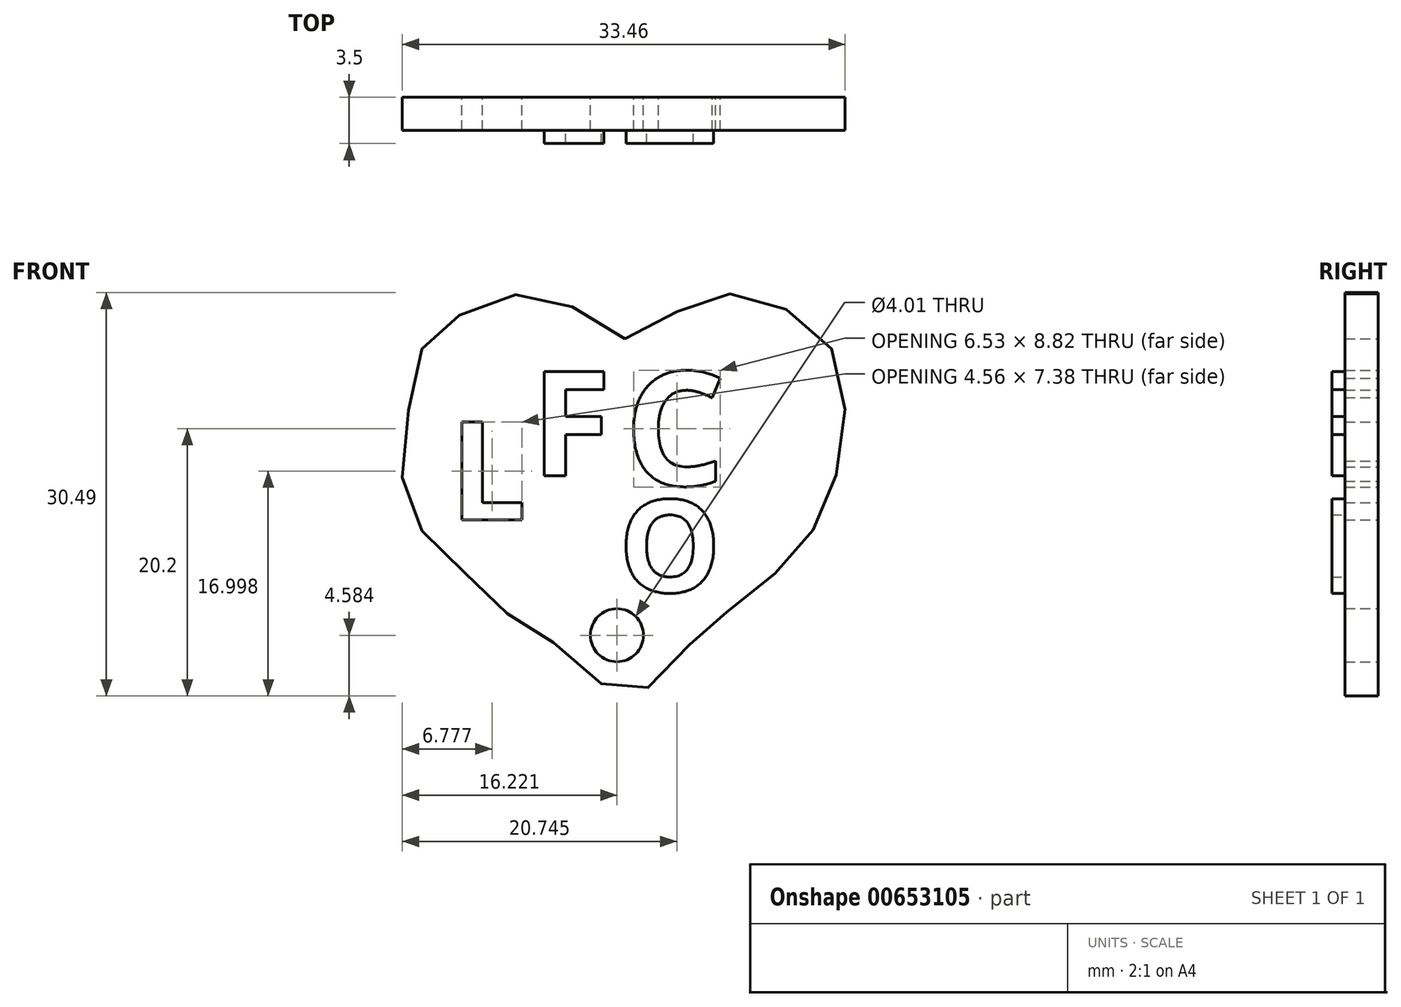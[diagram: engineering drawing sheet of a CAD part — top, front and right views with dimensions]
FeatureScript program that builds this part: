
annotation { "Feature Type Name" : "Feature", "Feature Type Description" : "" }
export const myFeature = defineFeature(function(context is Context, id is Id, definition is map)
    precondition{}
    {
        {
            var Q0;
            Q0=qCreatedBy(makeId("Front.planeOp"),FACE);
            var sketch = newSketch(context, id + "F0", { "sketchPlane" : qUnion([Q0])});
            skPoint(sketch, "E0", {"position": v(-33.54, 35.19) * mm});
            skPoint(sketch, "E1", {"position": v(-38.94, 38.43) * mm});
            skPoint(sketch, "E2", {"position": v(-44.55, 37.56) * mm});
            skPoint(sketch, "E3", {"position": v(-48.44, 35.19) * mm});
            skPoint(sketch, "E4", {"position": v(-49.95, 29.14) * mm});
            skPoint(sketch, "E5", {"position": v(-49.95, 22.44) * mm});
            skPoint(sketch, "E6", {"position": v(-46.28, 18.12) * mm});
            skPoint(sketch, "E7", {"position": v(-42.18, 14.24) * mm});
            skPoint(sketch, "E8", {"position": v(-37.86, 11.43) * mm});
            skPoint(sketch, "E9", {"position": v(-33.32, 8.19) * mm});
            skPoint(sketch, "E10", {"position": v(-29.22, 11.43) * mm});
            skPoint(sketch, "E11", {"position": v(-26.2, 14.24) * mm});
            skPoint(sketch, "E12", {"position": v(-21.44, 18.12) * mm});
            skPoint(sketch, "E13", {"position": v(-18.42, 22.44) * mm});
            skPoint(sketch, "E14", {"position": v(-16.9, 29.14) * mm});
            skPoint(sketch, "E15", {"position": v(-18.42, 35.19) * mm});
            skPoint(sketch, "E16", {"position": v(-28.35, 38) * mm});
            skPoint(sketch, "E17", {"position": v(-23.6, 38.21) * mm});
            skFitSpline(sketch, "E18", {"points": [v(-33.54, 35.19) * mm, v(-38.94, 38.43) * mm, v(-44.55, 37.56) * mm, v(-48.44, 35.19) * mm, v(-49.95, 29.14) * mm, v(-49.95, 22.44) * mm, v(-46.28, 18.12) * mm, v(-42.18, 14.24) * mm, v(-37.86, 11.43) * mm, v(-33.32, 8.19) * mm, v(-29.22, 11.43) * mm, v(-26.2, 14.24) * mm, v(-21.44, 18.12) * mm, v(-18.42, 22.44) * mm, v(-16.9, 29.14) * mm, v(-18.42, 35.19) * mm, v(-23.6, 38.21) * mm, v(-28.35, 38) * mm, v(-33.54, 35.19) * mm]});
            skSolve(sketch);
        }
        {
            var Q0;
            Q0 = qSketchRegion(id + "F0", true);
            extrude(context, id + "F1", {"entities" : qUnion([Q0]), "depth" : 2.5 * mm, "offsetDistance" : 25.4 * mm});
        }
        {
            var Q0;
            Q0=qCreatedBy(makeId("Front.planeOp"),FACE);
            var sketch = newSketch(context, id + "F2", { "sketchPlane" : qUnion([Q0])});
            skText(sketch, "E19", { "text": "F", "fontName": "OpenSans-Bold.ttf"});
            const initialGuessF2  = {"E19": [-0.04063, 0.02482, 1, 0, 0.00796]};
            skSetInitialGuess(sketch, initialGuessF2);
            skSolve(sketch);
        }
        {
            var Q0;
            Q0 = qSketchRegion(id + "F2", true);
            extrude(context, id + "F3", {"entities" : qUnion([Q0]), "operationType" : NewBodyOperationType.ADD, "depth" : 3.5 * mm, "offsetDistance" : 25.4 * mm});
        }
        {
            var Q0;
            Q0=qCreatedBy(makeId("Front.planeOp"),FACE);
            var sketch = newSketch(context, id + "F4", { "sketchPlane" : qUnion([Q0])});
            skText(sketch, "E20", { "text": "L", "fontName": "OpenSans-Bold.ttf"});
            const initialGuessF4  = {"E20": [-0.04678, 0.0215, 1, 0, 0.00744]};
            skSetInitialGuess(sketch, initialGuessF4);
            skSolve(sketch);
        }
        {
            var Q0;
            Q0 = qSketchRegion(id + "F4", true);
            extrude(context, id + "F5", {"entities" : qUnion([Q0]), "operationType" : NewBodyOperationType.REMOVE, "endBound" : BoundingType.UP_TO_NEXT, "depth" : 25.4 * mm, "offsetDistance" : 25.4 * mm});
        }
        {
            var Q0;
            Q0=qCreatedBy(makeId("Front.planeOp"),FACE);
            var sketch = newSketch(context, id + "F6", { "sketchPlane" : qUnion([Q0])});
            skText(sketch, "E21", { "text": "C", "fontName": "OpenSans-Bold.ttf"});
            const initialGuessF6  = {"E21": [-0.03357, 0.0241, 1, 0, 0.00865]};
            skSetInitialGuess(sketch, initialGuessF6);
            skSolve(sketch);
        }
        {
            var Q0;
            Q0 = qSketchRegion(id + "F6", true);
            extrude(context, id + "F7", {"entities" : qUnion([Q0]), "operationType" : NewBodyOperationType.REMOVE, "endBound" : BoundingType.UP_TO_NEXT, "depth" : 25.4 * mm, "offsetDistance" : 25.4 * mm});
        }
        {
            var Q0;
            Q0=qCreatedBy(makeId("Front.planeOp"),FACE);
            var sketch = newSketch(context, id + "F8", { "sketchPlane" : qUnion([Q0])});
            skText(sketch, "E22", { "text": "O", "fontName": "OpenSans-Bold.ttf"});
            const initialGuessF8  = {"E22": [-0.034, 0.01603, 1, 0, 0.00701]};
            skSetInitialGuess(sketch, initialGuessF8);
            skSolve(sketch);
        }
        {
            var Q0;
            Q0 = qSketchRegion(id + "F8", true);
            extrude(context, id + "F9", {"entities" : qUnion([Q0]), "operationType" : NewBodyOperationType.ADD, "depth" : 3.5 * mm, "offsetDistance" : 25.4 * mm});
        }
        {
            var Q0;
            Q0=qCreatedBy(makeId("Front.planeOp"),FACE);
            var sketch = newSketch(context, id + "F10", { "sketchPlane" : qUnion([Q0])});
            skCircle(sketch, "E23", {"center": v(-34.13, 12.77) * mm, "radius": 2 * mm});
            skSolve(sketch);
        }
        {
            var Q0;
            Q0 = qSketchRegion(id + "F10", true);
            extrude(context, id + "F11", {"entities" : qUnion([Q0]), "operationType" : NewBodyOperationType.REMOVE, "endBound" : BoundingType.UP_TO_NEXT, "depth" : 25.4 * mm, "offsetDistance" : 25.4 * mm});
        }
    });
